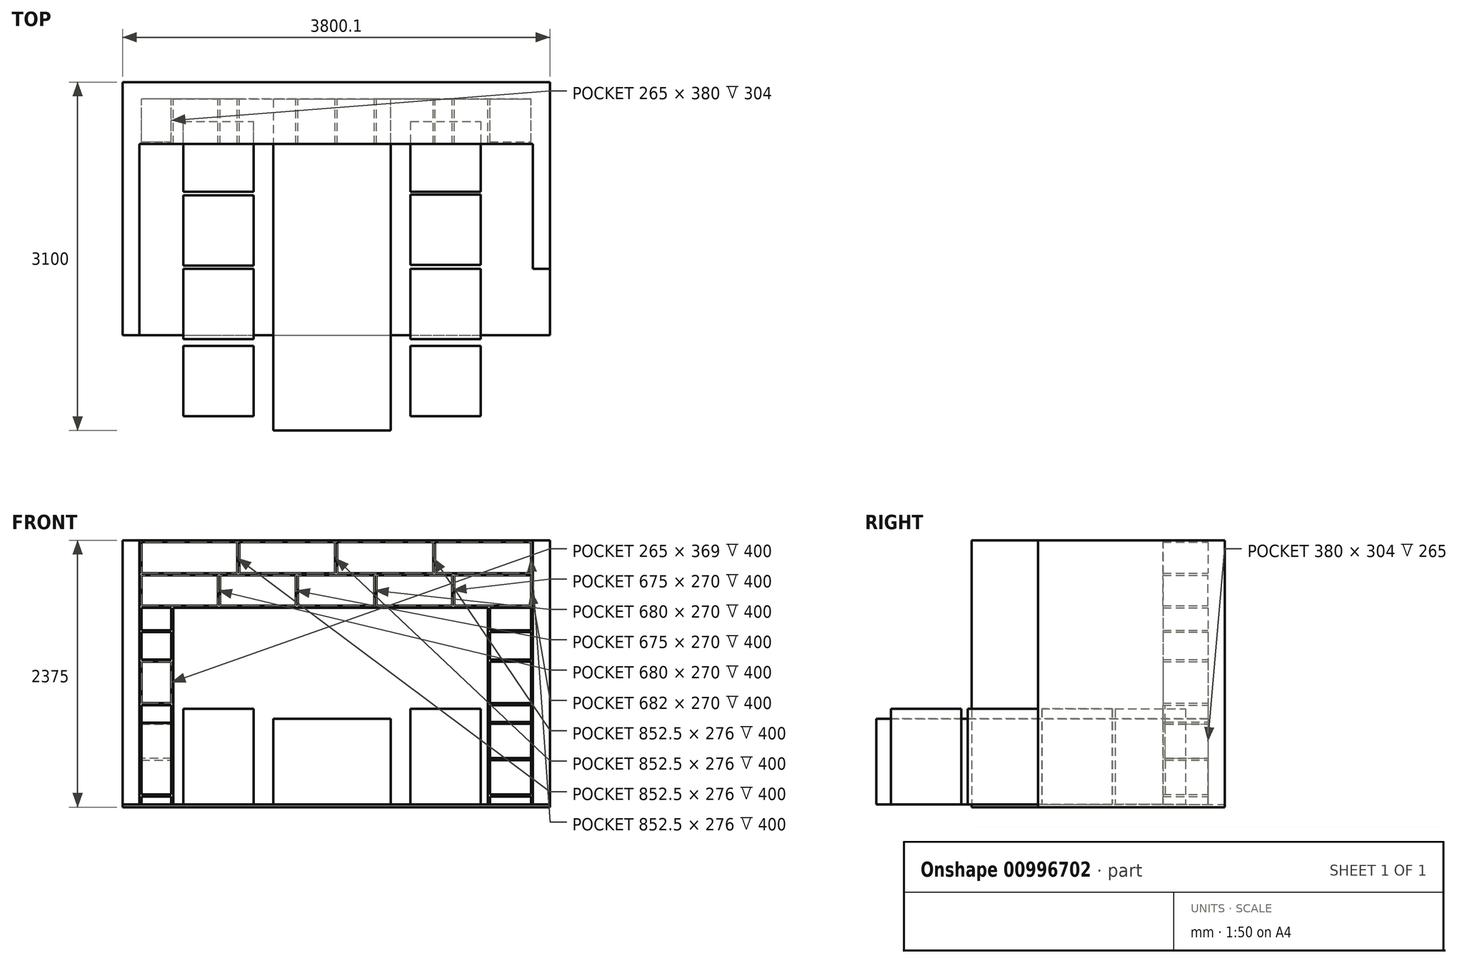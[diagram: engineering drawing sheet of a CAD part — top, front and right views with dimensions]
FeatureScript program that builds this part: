
annotation { "Feature Type Name" : "Feature", "Feature Type Description" : "" }
export const myFeature = defineFeature(function(context is Context, id is Id, definition is map)
    precondition{}
    {
        {
            var Q0;
            Q0=qCreatedBy(makeId("Top.planeOp"),FACE);
            var sketch = newSketch(context, id + "F0", { "sketchPlane" : qUnion([Q0])});
            skLineSegment(sketch, "E0", {"start": v(0, 0) * mm, "end": v(-1750, 0) * mm});
            skLineSegment(sketch, "E1", {"start": v(0, 0) * mm, "end": v(1750, 0) * mm});
            skLineSegment(sketch, "E2", {"start": v(-1750, 0) * mm, "end": v(-1750, -2100) * mm});
            skLineSegment(sketch, "E3", {"start": v(1750, 0) * mm, "end": v(1750, -1510) * mm});
            skLineSegment(sketch, "E4", {"start": v(-1750, -2100) * mm, "end": v(-1900, -2100) * mm});
            skLineSegment(sketch, "E5", {"start": v(-1900, -2100) * mm, "end": v(-1900, 150) * mm});
            skLineSegment(sketch, "E6", {"start": v(-1900, 150) * mm, "end": v(1900, 150) * mm});
            skLineSegment(sketch, "E7", {"start": v(1900, 150) * mm, "end": v(1900, -1510) * mm});
            skLineSegment(sketch, "E8", {"start": v(1900, -1510) * mm, "end": v(1750, -1510) * mm});
            skSolve(sketch);
        }
        {
            var Q0;
            Q0 = qSketchRegion(id + "F0", true);
            extrude(context, id + "F1", {"entities" : qUnion([Q0]), "depth" : 2375 * mm, "offsetDistance" : 25 * mm});
        }
        {
            var Q0;
            Q0=makeQuery(id+"F0.imprint","IMPRINT",FACE,{"disambiguationData":[TD([[makeQuery(id+"F0.imprint","IMPRINT",EDGE,{"derivedFrom":sQuery(id+"F0.wireOp",EDGE,"E0")}),-1.0]])]});
            var sketch = newSketch(context, id + "F2", { "sketchPlane" : qUnion([Q0])});
            skLineSegment(sketch, "E9.bottom", {"start": v(-1900.1, -2100.2) * mm, "end": v(1899.9, -2100.2) * mm});
            skLineSegment(sketch, "E9.top", {"start": v(-1900.1, 149.8) * mm, "end": v(1899.9, 149.8) * mm});
            skLineSegment(sketch, "E9.left", {"start": v(-1900.1, -2100.2) * mm, "end": v(-1900.1, 149.8) * mm});
            skLineSegment(sketch, "E9.right", {"start": v(1899.9, -2100.2) * mm, "end": v(1899.9, 149.8) * mm});
            skSolve(sketch);
        }
        {
            var Q0;
            {var subQ2=sQuery(id+"F2.wireOp",EDGE,"E9.bottom");Q0=makeQuery(id+"F2.imprint","IMPRINT",FACE,{"disambiguationData":[TD([[makeQuery(id+"F2.imprint","IMPRINT",EDGE,{"derivedFrom":subQ2}),1.0]])]});}
            extrude(context, id + "F3", {"entities" : qUnion([Q0]), "operationType" : NewBodyOperationType.ADD, "depth" : 25 * mm, "offsetDistance" : 25 * mm});
        }
        {
            var Q0;
            Q0=makeQuery(id+"F3.opExtrude","CAP_FACE",FACE,{"disambiguationData":[OSD([sQuery(id+"F0.wireOp",EDGE,"E0"),sQuery(id+"F0.wireOp",EDGE,"E1"),sQuery(id+"F0.wireOp",EDGE,"E2"),sQuery(id+"F0.wireOp",EDGE,"E3"),sQuery(id+"F0.wireOp",EDGE,"E4"),sQuery(id+"F0.wireOp",EDGE,"E5"),sQuery(id+"F0.wireOp",EDGE,"E8"),sQuery(id+"F2.wireOp",EDGE,"E9.bottom"),sQuery(id+"F2.wireOp",EDGE,"E9.top"),sQuery(id+"F2.wireOp",EDGE,"E9.left"),sQuery(id+"F2.wireOp",EDGE,"E9.right")])],"isStart":false});
            var sketch = newSketch(context, id + "F4", { "sketchPlane" : qUnion([Q0])});
            skLineSegment(sketch, "E10", {"start": v(-560, 0) * mm, "end": v(-560, -2950) * mm});
            skLineSegment(sketch, "E11", {"start": v(-560, -2950) * mm, "end": v(485, -2950) * mm});
            skLineSegment(sketch, "E12", {"start": v(485, -2950) * mm, "end": v(485, 0) * mm});
            skLineSegment(sketch, "E13", {"start": v(485, 0) * mm, "end": v(-560, 0) * mm});
            skSolve(sketch);
        }
        {
            var Q0;
            {var subQ0=sQuery(id+"F4.wireOp",EDGE,"E13");Q0=makeQuery(id+"F4.imprint","IMPRINT",FACE,{"disambiguationData":[TD([[makeQuery(id+"F4.imprint","IMPRINT",EDGE,{"derivedFrom":subQ0}),-1.0]])]});}
            var Q1;
            {var subQ0=sQuery(id+"F4.wireOp",EDGE,"E11");Q1=makeQuery(id+"F4.imprint","IMPRINT",FACE,{"disambiguationData":[TD([[makeQuery(id+"F4.imprint","IMPRINT",EDGE,{"derivedFrom":subQ0}),1.0]])]});}
            extrude(context, id + "F5", {"entities" : qUnion([Q0, Q1]), "operationType" : NewBodyOperationType.ADD, "depth" : 760 * mm, "offsetDistance" : 25 * mm});
        }
        {
            var Q0;
            {var subQ0=sQuery(id+"F0.wireOp",EDGE,"E5");var subQ2=sQuery(id+"F0.wireOp",EDGE,"E2");var subQ3=sQuery(id+"F0.wireOp",EDGE,"E4");var subQ4=sQuery(id+"F2.wireOp",EDGE,"E9.left");var subQ5=sQuery(id+"F0.wireOp",EDGE,"E1");var subQ6=sQuery(id+"F0.wireOp",EDGE,"E0");var subQ7=sQuery(id+"F2.wireOp",EDGE,"E9.bottom");var subQ8=sQuery(id+"F2.wireOp",EDGE,"E9.top");Q0=makeQuery(id+"F5.boolean.opBoolean","SPLIT",FACE,{"disambiguationData":[TD([makeQuery(id+"F1.opExtrude","SWEPT_FACE",FACE,{"disambiguationData":[OSD([subQ2])]})])],"derivedFrom":makeQuery(id+"F3.opExtrude","CAP_FACE",FACE,{"disambiguationData":[OSD([subQ6,subQ5,subQ2,sQuery(id+"F0.wireOp",EDGE,"E3"),subQ3,subQ0,sQuery(id+"F0.wireOp",EDGE,"E8"),subQ7,subQ8,subQ4,sQuery(id+"F2.wireOp",EDGE,"E9.right")])],"isStart":false})});}
            var sketch = newSketch(context, id + "F6", { "sketchPlane" : qUnion([Q0])});
            skLineSegment(sketch, "E14.bottom", {"start": v(-735, -2820) * mm, "end": v(-1360, -2820) * mm});
            skLineSegment(sketch, "E14.top", {"start": v(-735, -2195) * mm, "end": v(-1360, -2195) * mm});
            skLineSegment(sketch, "E14.left", {"start": v(-735, -2820) * mm, "end": v(-735, -2195) * mm});
            skLineSegment(sketch, "E14.right", {"start": v(-1360, -2820) * mm, "end": v(-1360, -2195) * mm});
            skLineSegment(sketch, "E15.bottom", {"start": v(-1360, -2135) * mm, "end": v(-735, -2135) * mm});
            skLineSegment(sketch, "E15.top", {"start": v(-1360, -1510) * mm, "end": v(-735, -1510) * mm});
            skLineSegment(sketch, "E15.left", {"start": v(-1360, -2135) * mm, "end": v(-1360, -1510) * mm});
            skLineSegment(sketch, "E15.right", {"start": v(-735, -2135) * mm, "end": v(-735, -1510) * mm});
            skLineSegment(sketch, "E16.bottom", {"start": v(-1360, -1480) * mm, "end": v(-735, -1480) * mm});
            skLineSegment(sketch, "E16.top", {"start": v(-1360, -855) * mm, "end": v(-735, -855) * mm});
            skLineSegment(sketch, "E16.left", {"start": v(-1360, -1480) * mm, "end": v(-1360, -855) * mm});
            skLineSegment(sketch, "E16.right", {"start": v(-735, -1480) * mm, "end": v(-735, -855) * mm});
            skLineSegment(sketch, "E17.bottom", {"start": v(-1360, -825) * mm, "end": v(-735, -825) * mm});
            skLineSegment(sketch, "E17.top", {"start": v(-1360, -200) * mm, "end": v(-735, -200) * mm});
            skLineSegment(sketch, "E17.left", {"start": v(-1360, -825) * mm, "end": v(-1360, -200) * mm});
            skLineSegment(sketch, "E17.right", {"start": v(-735, -825) * mm, "end": v(-735, -200) * mm});
            skLineSegment(sketch, "E18.bottom", {"start": v(660, -200) * mm, "end": v(1285, -200) * mm});
            skLineSegment(sketch, "E18.top", {"start": v(660, -825) * mm, "end": v(1285, -825) * mm});
            skLineSegment(sketch, "E18.left", {"start": v(660, -200) * mm, "end": v(660, -825) * mm});
            skLineSegment(sketch, "E18.right", {"start": v(1285, -200) * mm, "end": v(1285, -825) * mm});
            skLineSegment(sketch, "E19.bottom", {"start": v(660, -850) * mm, "end": v(1285, -850) * mm});
            skLineSegment(sketch, "E19.top", {"start": v(660, -1475) * mm, "end": v(1285, -1475) * mm});
            skLineSegment(sketch, "E19.left", {"start": v(660, -850) * mm, "end": v(660, -1475) * mm});
            skLineSegment(sketch, "E19.right", {"start": v(1285, -850) * mm, "end": v(1285, -1475) * mm});
            skLineSegment(sketch, "E20.bottom", {"start": v(660, -1510) * mm, "end": v(1285, -1510) * mm});
            skLineSegment(sketch, "E20.top", {"start": v(660, -2135) * mm, "end": v(1285, -2135) * mm});
            skLineSegment(sketch, "E20.left", {"start": v(660, -1510) * mm, "end": v(660, -2135) * mm});
            skLineSegment(sketch, "E20.right", {"start": v(1285, -1510) * mm, "end": v(1285, -2135) * mm});
            skLineSegment(sketch, "E21.bottom", {"start": v(660, -2195) * mm, "end": v(1285, -2195) * mm});
            skLineSegment(sketch, "E21.top", {"start": v(660, -2820) * mm, "end": v(1285, -2820) * mm});
            skLineSegment(sketch, "E21.left", {"start": v(660, -2195) * mm, "end": v(660, -2820) * mm});
            skLineSegment(sketch, "E21.right", {"start": v(1285, -2195) * mm, "end": v(1285, -2820) * mm});
            skSolve(sketch);
        }
        {
            var Q0;
            Q0 = qSketchRegion(id + "F6", true);
            extrude(context, id + "F7", {"entities" : qUnion([Q0]), "operationType" : NewBodyOperationType.ADD, "depth" : 850 * mm, "offsetDistance" : 25 * mm});
        }
        {
            var Q0;
            Q0=makeQuery(id+"F1.opExtrude","SWEPT_FACE",FACE,{"disambiguationData":[OSD([sQuery(id+"F0.wireOp",EDGE,"E0"),sQuery(id+"F0.wireOp",EDGE,"E1")])]});
            var sketch = newSketch(context, id + "F8", { "sketchPlane" : qUnion([Q0])});
            skLineSegment(sketch, "E22", {"start": v(-1750, 2375) * mm, "end": v(1750, 2375) * mm});
            skLineSegment(sketch, "E23", {"start": v(1750, 2375) * mm, "end": v(1750, 2357) * mm});
            skLineSegment(sketch, "E24", {"start": v(1750, 2357) * mm, "end": v(-1750, 2357) * mm});
            skLineSegment(sketch, "E25", {"start": v(-1750, 2357) * mm, "end": v(-1750, 2375) * mm});
            skLineSegment(sketch, "E26", {"start": v(-1750, 1775) * mm, "end": v(1750, 1775) * mm});
            skLineSegment(sketch, "E27", {"start": v(1750, 1775) * mm, "end": v(1750, 1793) * mm});
            skLineSegment(sketch, "E28", {"start": v(1750, 1793) * mm, "end": v(-1750, 1793) * mm});
            skLineSegment(sketch, "E29", {"start": v(-1750, 1793) * mm, "end": v(-1750, 1775) * mm});
            skLineSegment(sketch, "E30.bottom", {"start": v(-1467, 1775) * mm, "end": v(-1449, 1775) * mm});
            skLineSegment(sketch, "E30.top", {"start": v(-1467, 25) * mm, "end": v(-1449, 25) * mm});
            skLineSegment(sketch, "E30.left", {"start": v(-1467, 1775) * mm, "end": v(-1467, 25) * mm});
            skLineSegment(sketch, "E30.right", {"start": v(-1449, 1775) * mm, "end": v(-1449, 25) * mm});
            skLineSegment(sketch, "E31.bottom", {"start": v(1349, 1775) * mm, "end": v(1367, 1775) * mm});
            skLineSegment(sketch, "E31.top", {"start": v(1349, 25) * mm, "end": v(1367, 25) * mm});
            skLineSegment(sketch, "E31.left", {"start": v(1349, 1775) * mm, "end": v(1349, 25) * mm});
            skLineSegment(sketch, "E31.right", {"start": v(1367, 1775) * mm, "end": v(1367, 25) * mm});
            skLineSegment(sketch, "E32.bottom", {"start": v(-1750, 25) * mm, "end": v(-1732, 25) * mm});
            skLineSegment(sketch, "E32.top", {"start": v(-1750, 1775) * mm, "end": v(-1732, 1775) * mm});
            skLineSegment(sketch, "E32.left", {"start": v(-1750, 25) * mm, "end": v(-1750, 1775) * mm});
            skLineSegment(sketch, "E32.right", {"start": v(-1732, 25) * mm, "end": v(-1732, 1775) * mm});
            skLineSegment(sketch, "E33.bottom", {"start": v(1750, 25) * mm, "end": v(1732, 25) * mm});
            skLineSegment(sketch, "E33.top", {"start": v(1750, 1775) * mm, "end": v(1732, 1775) * mm});
            skLineSegment(sketch, "E33.left", {"start": v(1750, 25) * mm, "end": v(1750, 1775) * mm});
            skLineSegment(sketch, "E33.right", {"start": v(1732, 25) * mm, "end": v(1732, 1775) * mm});
            skLineSegment(sketch, "E34.bottom", {"start": v(1750, 1793) * mm, "end": v(1732, 1793) * mm});
            skLineSegment(sketch, "E34.top", {"start": v(1750, 2357) * mm, "end": v(1732, 2357) * mm});
            skLineSegment(sketch, "E34.left", {"start": v(1750, 1793) * mm, "end": v(1750, 2357) * mm});
            skLineSegment(sketch, "E34.right", {"start": v(1732, 1793) * mm, "end": v(1732, 2357) * mm});
            skLineSegment(sketch, "E35.bottom", {"start": v(-1732, 1793) * mm, "end": v(-1750, 1793) * mm});
            skLineSegment(sketch, "E35.top", {"start": v(-1732, 2375) * mm, "end": v(-1750, 2375) * mm});
            skLineSegment(sketch, "E35.left", {"start": v(-1732, 1793) * mm, "end": v(-1732, 2375) * mm});
            skLineSegment(sketch, "E35.right", {"start": v(-1750, 1793) * mm, "end": v(-1750, 2375) * mm});
            skSolve(sketch);
        }
        {
            var Q0;
            {var subQ6=sQuery(id+"F8.wireOp",EDGE,"E34.left");var subQ8=sQuery(id+"F8.wireOp",EDGE,"E23");var subQ13=sQuery(id+"F8.wireOp",EDGE,"E27");var subQ25=sQuery(id+"F8.wireOp",EDGE,"E35.right");var subQ26=sQuery(id+"F8.wireOp",EDGE,"E25");Q0=qUnion([makeQuery(id+"F8.imprint","IMPRINT",FACE,{"disambiguationData":[TD([[makeQuery(id+"F8.imprint","IMPRINT",EDGE,{"derivedFrom":subQ13}),-1.0]])]}),makeQuery(id+"F8.imprint","IMPRINT",FACE,{"disambiguationData":[TD([[makeQuery(id+"F8.imprint","IMPRINT",EDGE,{"derivedFrom":subQ8}),-1.0]])]}),makeQuery(id+"F8.imprint","IMPRINT",FACE,{"disambiguationData":[TD([[makeQuery(id+"F8.imprint","IMPRINT",EDGE,{"derivedFrom":sQuery(id+"F8.wireOp",EDGE,"E30.top")}),1.0]])]}),makeQuery(id+"F8.imprint","IMPRINT",FACE,{"disambiguationData":[TD([[makeQuery(id+"F8.imprint","IMPRINT",EDGE,{"derivedFrom":subQ26}),1.0]])]}),makeQuery(id+"F8.imprint","IMPRINT",FACE,{"disambiguationData":[TD([[makeQuery(id+"F8.imprint","IMPRINT",EDGE,{"derivedFrom":subQ25}),1.0]])]}),makeQuery(id+"F8.imprint","IMPRINT",FACE,{"disambiguationData":[TD([[makeQuery(id+"F8.imprint","IMPRINT",EDGE,{"derivedFrom":sQuery(id+"F8.wireOp",EDGE,"E31.top")}),1.0]])]}),makeQuery(id+"F8.imprint","IMPRINT",FACE,{"disambiguationData":[TD([[makeQuery(id+"F8.imprint","IMPRINT",EDGE,{"derivedFrom":sQuery(id+"F8.wireOp",EDGE,"E33.bottom")}),1.0]])]}),makeQuery(id+"F8.imprint","IMPRINT",FACE,{"disambiguationData":[TD([[makeQuery(id+"F8.imprint","IMPRINT",EDGE,{"derivedFrom":subQ6}),-1.0]])]}),makeQuery(id+"F8.imprint","IMPRINT",FACE,{"disambiguationData":[TD([[makeQuery(id+"F8.imprint","IMPRINT",EDGE,{"derivedFrom":sQuery(id+"F8.wireOp",EDGE,"E32.bottom")}),1.0]])]})]);}
            extrude(context, id + "F9", {"entities" : qUnion([Q0]), "operationType" : NewBodyOperationType.ADD, "depth" : 400 * mm, "offsetDistance" : 25 * mm});
        }
        {
            var Q0;
            Q0=makeQuery(id+"F9.boolean.opBoolean","SPLIT",FACE,{"disambiguationData":[TD([makeQuery(id+"F9.opExtrude","SWEPT_FACE",FACE,{"disambiguationData":[OSD([sQuery(id+"F8.wireOp",EDGE,"E24")])]})])],"derivedFrom":makeQuery(id+"F1.opExtrude","SWEPT_FACE",FACE,{"disambiguationData":[OSD([sQuery(id+"F0.wireOp",EDGE,"E0"),sQuery(id+"F0.wireOp",EDGE,"E1")])]})});
            var sketch = newSketch(context, id + "F10", { "sketchPlane" : qUnion([Q0])});
            skLineSegment(sketch, "E36", {"start": v(1732, 2075) * mm, "end": v(1732, 2081) * mm});
            skLineSegment(sketch, "E37", {"start": v(1732, 2081) * mm, "end": v(-1732, 2081) * mm});
            skLineSegment(sketch, "E38", {"start": v(-1732, 2081) * mm, "end": v(-1732, 2063) * mm});
            skLineSegment(sketch, "E39", {"start": v(-1732, 2063) * mm, "end": v(1732, 2063) * mm});
            skLineSegment(sketch, "E40", {"start": v(1732, 2063) * mm, "end": v(1732, 2081) * mm});
            skSolve(sketch);
        }
        {
            var Q0;
            {var subQ0=sQuery(id+"F10.wireOp",EDGE,"E37");Q0=makeQuery(id+"F10.imprint","IMPRINT",FACE,{"disambiguationData":[TD([[makeQuery(id+"F10.imprint","IMPRINT",EDGE,{"derivedFrom":subQ0}),1.0]])]});}
            extrude(context, id + "F11", {"entities" : qUnion([Q0]), "operationType" : NewBodyOperationType.ADD, "depth" : 400 * mm, "offsetDistance" : 25 * mm});
        }
        {
            var Q0;
            {var subQ0=makeQuery(id+"F9.opExtrude","SWEPT_FACE",FACE,{"disambiguationData":[OSD([sQuery(id+"F8.wireOp",EDGE,"E24")])]});Q0=makeQuery(id+"F11.boolean.opBoolean","SPLIT",FACE,{"disambiguationData":[TD([subQ0])],"derivedFrom":makeQuery(id+"F9.boolean.opBoolean","SPLIT",FACE,{"disambiguationData":[TD([subQ0])],"derivedFrom":makeQuery(id+"F1.opExtrude","SWEPT_FACE",FACE,{"disambiguationData":[OSD([sQuery(id+"F0.wireOp",EDGE,"E0"),sQuery(id+"F0.wireOp",EDGE,"E1")])]})})});}
            var sketch = newSketch(context, id + "F12", { "sketchPlane" : qUnion([Q0])});
            skLineSegment(sketch, "E41", {"start": v(0, 2081) * mm, "end": v(9, 2081) * mm});
            skLineSegment(sketch, "E42", {"start": v(9, 2081) * mm, "end": v(9, 2357) * mm});
            skLineSegment(sketch, "E43", {"start": v(9, 2357) * mm, "end": v(-9, 2357) * mm});
            skLineSegment(sketch, "E44", {"start": v(-9, 2357) * mm, "end": v(-9, 2081) * mm});
            skLineSegment(sketch, "E45", {"start": v(-9, 2081) * mm, "end": v(9, 2081) * mm});
            skLineSegment(sketch, "E46", {"start": v(-879.5, 2357) * mm, "end": v(-879.5, 2081) * mm});
            skLineSegment(sketch, "E47", {"start": v(-879.5, 2081) * mm, "end": v(-861.5, 2081) * mm});
            skLineSegment(sketch, "E48", {"start": v(-861.5, 2081) * mm, "end": v(-861.5, 2357) * mm});
            skLineSegment(sketch, "E49", {"start": v(-861.5, 2357) * mm, "end": v(-879.5, 2357) * mm});
            skLineSegment(sketch, "E50", {"start": v(879.5, 2081) * mm, "end": v(879.5, 2357) * mm});
            skLineSegment(sketch, "E51", {"start": v(879.5, 2357) * mm, "end": v(861.5, 2357) * mm});
            skLineSegment(sketch, "E52", {"start": v(861.5, 2357) * mm, "end": v(861.5, 2081) * mm});
            skLineSegment(sketch, "E53", {"start": v(861.5, 2081) * mm, "end": v(879.5, 2081) * mm});
            skSolve(sketch);
        }
        {
            var Q0;
            Q0 = qSketchRegion(id + "F12", true);
            extrude(context, id + "F13", {"entities" : qUnion([Q0]), "operationType" : NewBodyOperationType.ADD, "depth" : 400 * mm, "offsetDistance" : 25 * mm});
        }
        {
            var Q0;
            {var subQ0=makeQuery(id+"F9.opExtrude","SWEPT_FACE",FACE,{"disambiguationData":[OSD([sQuery(id+"F8.wireOp",EDGE,"E28")])]});Q0=makeQuery(id+"F11.boolean.opBoolean","SPLIT",FACE,{"disambiguationData":[TD([subQ0])],"derivedFrom":makeQuery(id+"F9.boolean.opBoolean","SPLIT",FACE,{"disambiguationData":[TD([makeQuery(id+"F9.opExtrude","SWEPT_FACE",FACE,{"disambiguationData":[OSD([sQuery(id+"F8.wireOp",EDGE,"E24")])]})])],"derivedFrom":makeQuery(id+"F1.opExtrude","SWEPT_FACE",FACE,{"disambiguationData":[OSD([sQuery(id+"F0.wireOp",EDGE,"E0"),sQuery(id+"F0.wireOp",EDGE,"E1")])]})})});}
            var sketch = newSketch(context, id + "F14", { "sketchPlane" : qUnion([Q0])});
            skLineSegment(sketch, "E54", {"start": v(1032, 1793) * mm, "end": v(847.37, 1793) * mm});
            skLineSegment(sketch, "E55", {"start": v(1032, 1793) * mm, "end": v(1032, 2063) * mm});
            skLineSegment(sketch, "E56", {"start": v(1032, 2063) * mm, "end": v(1050, 2063) * mm});
            skLineSegment(sketch, "E57", {"start": v(1050, 2063) * mm, "end": v(1050, 1793) * mm});
            skLineSegment(sketch, "E58", {"start": v(1050, 1793) * mm, "end": v(1032, 1793) * mm});
            skLineSegment(sketch, "E59", {"start": v(-866, 1793) * mm, "end": v(-1052, 1793) * mm});
            skLineSegment(sketch, "E60", {"start": v(-1052, 1793) * mm, "end": v(-1052, 2063) * mm});
            skLineSegment(sketch, "E61", {"start": v(-1052, 2063) * mm, "end": v(-1034, 2063) * mm});
            skLineSegment(sketch, "E62", {"start": v(-1034, 2063) * mm, "end": v(-1034, 1793) * mm});
            skLineSegment(sketch, "E63", {"start": v(-1034, 1793) * mm, "end": v(-1052, 1793) * mm});
            skLineSegment(sketch, "E64", {"start": v(-341, 2063) * mm, "end": v(-341, 1793) * mm});
            skLineSegment(sketch, "E65", {"start": v(-341, 1793) * mm, "end": v(-359, 1793) * mm});
            skLineSegment(sketch, "E66", {"start": v(-359, 1793) * mm, "end": v(-359, 2063) * mm});
            skLineSegment(sketch, "E67", {"start": v(-359, 2063) * mm, "end": v(-341, 2063) * mm});
            skLineSegment(sketch, "E68", {"start": v(339, 2063) * mm, "end": v(339, 1793) * mm});
            skLineSegment(sketch, "E69", {"start": v(339, 1793) * mm, "end": v(357, 1793) * mm});
            skLineSegment(sketch, "E70", {"start": v(357, 1793) * mm, "end": v(357, 2063) * mm});
            skLineSegment(sketch, "E71", {"start": v(357, 2063) * mm, "end": v(339, 2063) * mm});
            skSolve(sketch);
        }
        {
            var Q0;
            {var subQ0=sQuery(id+"F14.wireOp",EDGE,"E60");Q0=qUnion([makeQuery(id+"F14.imprint","IMPRINT",FACE,{"disambiguationData":[TD([[makeQuery(id+"F14.imprint","IMPRINT",EDGE,{"derivedFrom":sQuery(id+"F14.wireOp",EDGE,"E55")}),-1.0]])]}),makeQuery(id+"F14.imprint","IMPRINT",FACE,{"disambiguationData":[TD([[makeQuery(id+"F14.imprint","IMPRINT",EDGE,{"derivedFrom":subQ0}),-1.0]])]}),makeQuery(id+"F14.imprint","IMPRINT",FACE,{"disambiguationData":[TD([[makeQuery(id+"F14.imprint","IMPRINT",EDGE,{"derivedFrom":sQuery(id+"F14.wireOp",EDGE,"E64")}),-1.0]])]}),makeQuery(id+"F14.imprint","IMPRINT",FACE,{"disambiguationData":[TD([[makeQuery(id+"F14.imprint","IMPRINT",EDGE,{"derivedFrom":sQuery(id+"F14.wireOp",EDGE,"E68")}),1.0]])]})]);}
            extrude(context, id + "F15", {"entities" : qUnion([Q0]), "operationType" : NewBodyOperationType.ADD, "depth" : 400 * mm, "offsetDistance" : 25 * mm});
        }
        {
            var Q0;
            {var subQ0=sQuery(id+"F0.wireOp",EDGE,"E1");var subQ1=sQuery(id+"F0.wireOp",EDGE,"E0");var subQ4=sQuery(id+"F8.wireOp",EDGE,"E30.left");Q0=makeQuery(id+"F9.boolean.opBoolean","SPLIT",FACE,{"disambiguationData":[TD([makeQuery(id+"F9.opExtrude","SWEPT_FACE",FACE,{"disambiguationData":[OSD([subQ4])]})])],"derivedFrom":makeQuery(id+"F1.opExtrude","SWEPT_FACE",FACE,{"disambiguationData":[OSD([subQ1,subQ0])]})});}
            var sketch = newSketch(context, id + "F16", { "sketchPlane" : qUnion([Q0])});
            skPoint(sketch, "E72", {"position": v(-1467, 925) * mm});
            skLineSegment(sketch, "E73", {"start": v(-1467, 925) * mm, "end": v(-1732, 925) * mm});
            skLineSegment(sketch, "E74", {"start": v(-1732, 925) * mm, "end": v(-1732, 739) * mm});
            skLineSegment(sketch, "E75", {"start": v(-1732, 739) * mm, "end": v(-1467, 739) * mm});
            skLineSegment(sketch, "E76", {"start": v(-1467, 739) * mm, "end": v(-1467, 925) * mm});
            skLineSegment(sketch, "E77", {"start": v(-1732, 757) * mm, "end": v(-1467, 757) * mm});
            skLineSegment(sketch, "E78", {"start": v(-1467, 757) * mm, "end": v(-1467, 739) * mm});
            skLineSegment(sketch, "E79", {"start": v(-1732, 739) * mm, "end": v(-1732, 757) * mm});
            skLineSegment(sketch, "E80", {"start": v(-1732, 925) * mm, "end": v(-1732, 907) * mm});
            skLineSegment(sketch, "E81", {"start": v(-1732, 907) * mm, "end": v(-1467, 907) * mm});
            skLineSegment(sketch, "E82", {"start": v(-1467, 907) * mm, "end": v(-1467, 925) * mm});
            skLineSegment(sketch, "E83", {"start": v(-1467, 435) * mm, "end": v(-1732, 435) * mm});
            skLineSegment(sketch, "E84", {"start": v(-1732, 435) * mm, "end": v(-1732, 417) * mm});
            skLineSegment(sketch, "E85", {"start": v(-1732, 417) * mm, "end": v(-1467, 417) * mm});
            skLineSegment(sketch, "E86", {"start": v(-1467, 417) * mm, "end": v(-1467, 435) * mm});
            skLineSegment(sketch, "E87", {"start": v(-1732, 113) * mm, "end": v(-1467, 113) * mm});
            skLineSegment(sketch, "E88", {"start": v(-1467, 113) * mm, "end": v(-1467, 95) * mm});
            skLineSegment(sketch, "E89", {"start": v(-1467, 95) * mm, "end": v(-1732, 95) * mm});
            skLineSegment(sketch, "E90", {"start": v(-1732, 95) * mm, "end": v(-1732, 113) * mm});
            skSolve(sketch);
        }
        {
            var Q0;
            {var subQ0=sQuery(id+"F16.wireOp",EDGE,"E73");Q0=makeQuery(id+"F16.imprint","IMPRINT",FACE,{"disambiguationData":[TD([[makeQuery(id+"F16.imprint","IMPRINT",EDGE,{"derivedFrom":subQ0}),1.0]])]});}
            var Q1;
            {var subQ0=sQuery(id+"F16.wireOp",EDGE,"E75");Q1=makeQuery(id+"F16.imprint","IMPRINT",FACE,{"disambiguationData":[TD([[makeQuery(id+"F16.imprint","IMPRINT",EDGE,{"derivedFrom":subQ0}),1.0]])]});}
            var Q2;
            Q2=makeQuery(id+"F16.imprint","IMPRINT",FACE,{"disambiguationData":[TD([[makeQuery(id+"F16.imprint","IMPRINT",EDGE,{"derivedFrom":sQuery(id+"F16.wireOp",EDGE,"E83")}),1.0]])]});
            var Q3;
            Q3=makeQuery(id+"F16.imprint","IMPRINT",FACE,{"disambiguationData":[TD([[makeQuery(id+"F16.imprint","IMPRINT",EDGE,{"derivedFrom":sQuery(id+"F16.wireOp",EDGE,"E87")}),-1.0]])]});
            extrude(context, id + "F17", {"entities" : qUnion([Q0, Q1, Q2, Q3]), "operationType" : NewBodyOperationType.ADD, "depth" : 380 * mm, "offsetDistance" : 25 * mm});
        }
        {
            var Q0;
            Q0=makeQuery(id+"F17.opExtrude","CAP_FACE",FACE,{"disambiguationData":[OSD([sQuery(id+"F16.wireOp",EDGE,"E73"),sQuery(id+"F16.wireOp",EDGE,"E74"),sQuery(id+"F16.wireOp",EDGE,"E76"),sQuery(id+"F16.wireOp",EDGE,"E81")])],"isStart":false});
            var Q1;
            Q1=makeQuery(id+"F17.opExtrude","CAP_FACE",FACE,{"disambiguationData":[OSD([sQuery(id+"F16.wireOp",EDGE,"E87"),sQuery(id+"F16.wireOp",EDGE,"E88"),sQuery(id+"F16.wireOp",EDGE,"E89"),sQuery(id+"F16.wireOp",EDGE,"E90")])],"isStart":false});
            extrude(context, id + "F18", {"entities" : qUnion([Q0, Q1]), "operationType" : NewBodyOperationType.ADD, "depth" : 20 * mm, "offsetDistance" : 25 * mm});
        }
        {
            var Q0;
            {var subQ2=sQuery(id+"F8.wireOp",EDGE,"E30.left");var subQ4=makeQuery(id+"F9.opExtrude","SWEPT_FACE",FACE,{"disambiguationData":[OSD([subQ2])]});var subQ6=sQuery(id+"F0.wireOp",EDGE,"E1");var subQ7=sQuery(id+"F0.wireOp",EDGE,"E0");Q0=makeQuery(id+"F17.boolean.opBoolean","SPLIT",FACE,{"disambiguationData":[TD([makeQuery(id+"F17.opExtrude","SWEPT_FACE",FACE,{"disambiguationData":[OSD([sQuery(id+"F16.wireOp",EDGE,"E73")])]})])],"derivedFrom":makeQuery(id+"F9.boolean.opBoolean","SPLIT",FACE,{"disambiguationData":[TD([subQ4])],"derivedFrom":makeQuery(id+"F1.opExtrude","SWEPT_FACE",FACE,{"disambiguationData":[OSD([subQ7,subQ6])]})})});}
            var sketch = newSketch(context, id + "F19", { "sketchPlane" : qUnion([Q0])});
            skLineSegment(sketch, "E91", {"start": v(-1732, 1312) * mm, "end": v(-1467, 1312) * mm});
            skLineSegment(sketch, "E92", {"start": v(-1467, 1312) * mm, "end": v(-1467, 1294) * mm});
            skLineSegment(sketch, "E93", {"start": v(-1467, 1294) * mm, "end": v(-1732, 1294) * mm});
            skLineSegment(sketch, "E94", {"start": v(-1732, 1294) * mm, "end": v(-1732, 1312) * mm});
            skLineSegment(sketch, "E95", {"start": v(-1732, 1557) * mm, "end": v(-1467, 1557) * mm});
            skLineSegment(sketch, "E96", {"start": v(-1467, 1557) * mm, "end": v(-1467, 1575) * mm});
            skLineSegment(sketch, "E97", {"start": v(-1467, 1575) * mm, "end": v(-1732, 1575) * mm});
            skLineSegment(sketch, "E98", {"start": v(-1732, 1575) * mm, "end": v(-1732, 1557) * mm});
            skPoint(sketch, "E99", {"position": v(-1599.5, 1775) * mm});
            skPoint(sketch, "E100", {"position": v(-1599.5, 925) * mm});
            skSolve(sketch);
        }
        {
            var Q0;
            Q0 = qSketchRegion(id + "F19", true);
            extrude(context, id + "F20", {"entities" : qUnion([Q0]), "operationType" : NewBodyOperationType.ADD, "depth" : 400 * mm, "offsetDistance" : 25 * mm});
        }
        {
            var Q0;
            Q0=makeQuery(id+"F17.opExtrude","CAP_FACE",FACE,{"disambiguationData":[OSD([sQuery(id+"F16.wireOp",EDGE,"E74"),sQuery(id+"F16.wireOp",EDGE,"E75"),sQuery(id+"F16.wireOp",EDGE,"E76"),sQuery(id+"F16.wireOp",EDGE,"E77")])],"isStart":false});
            var sketch = newSketch(context, id + "F21", { "sketchPlane" : qUnion([Q0])});
            skPoint(sketch, "E101", {"position": v(-1732, 750.5) * mm});
            skPoint(sketch, "E102", {"position": v(-1732, 749) * mm});
            skPoint(sketch, "E103", {"position": v(-1732, 748) * mm});
            skLineSegment(sketch, "E104", {"start": v(-1732, 750.5) * mm, "end": v(-1467, 750.5) * mm});
            skLineSegment(sketch, "E105", {"start": v(-1467, 750.5) * mm, "end": v(-1467, 905.5) * mm});
            skLineSegment(sketch, "E106", {"start": v(-1467, 905.5) * mm, "end": v(-1732, 905.5) * mm});
            skLineSegment(sketch, "E107", {"start": v(-1732, 905.5) * mm, "end": v(-1732, 750.5) * mm});
            skLineSegment(sketch, "E108", {"start": v(-1732, 749) * mm, "end": v(-1467, 749) * mm});
            skLineSegment(sketch, "E109", {"start": v(-1467, 749) * mm, "end": v(-1467, 114) * mm});
            skLineSegment(sketch, "E110", {"start": v(-1467, 114) * mm, "end": v(-1732, 114) * mm});
            skLineSegment(sketch, "E111", {"start": v(-1732, 114) * mm, "end": v(-1732, 749) * mm});
            skSolve(sketch);
        }
        {
            var Q0;
            Q0 = qSketchRegion(id + "F21", true);
            extrude(context, id + "F22", {"entities" : qUnion([Q0]), "operationType" : NewBodyOperationType.ADD, "depth" : 18 * mm, "offsetDistance" : 25 * mm});
        }
        {
            var Q0;
            {var subQ0=sQuery(id+"F0.wireOp",EDGE,"E1");var subQ1=sQuery(id+"F0.wireOp",EDGE,"E0");var subQ2=sQuery(id+"F8.wireOp",EDGE,"E31.right");Q0=makeQuery(id+"F9.boolean.opBoolean","SPLIT",FACE,{"disambiguationData":[TD([makeQuery(id+"F9.opExtrude","SWEPT_FACE",FACE,{"disambiguationData":[OSD([subQ2])]})])],"derivedFrom":makeQuery(id+"F1.opExtrude","SWEPT_FACE",FACE,{"disambiguationData":[OSD([subQ1,subQ0])]})});}
            var sketch = newSketch(context, id + "F23", { "sketchPlane" : qUnion([Q0])});
            skLineSegment(sketch, "E112", {"start": v(1367, 1575) * mm, "end": v(1732, 1575) * mm});
            skLineSegment(sketch, "E113", {"start": v(1732, 1575) * mm, "end": v(1732, 1557) * mm});
            skLineSegment(sketch, "E114", {"start": v(1732, 1557) * mm, "end": v(1367, 1557) * mm});
            skLineSegment(sketch, "E115", {"start": v(1367, 1557) * mm, "end": v(1367, 1575) * mm});
            skLineSegment(sketch, "E116", {"start": v(1367, 1312) * mm, "end": v(1732, 1312) * mm});
            skLineSegment(sketch, "E117", {"start": v(1732, 1312) * mm, "end": v(1732, 1294) * mm});
            skLineSegment(sketch, "E118", {"start": v(1732, 1294) * mm, "end": v(1367, 1294) * mm});
            skLineSegment(sketch, "E119", {"start": v(1367, 1294) * mm, "end": v(1367, 1312) * mm});
            skLineSegment(sketch, "E120", {"start": v(1367, 95) * mm, "end": v(1732, 95) * mm});
            skLineSegment(sketch, "E121", {"start": v(1732, 95) * mm, "end": v(1732, 113) * mm});
            skLineSegment(sketch, "E122", {"start": v(1732, 113) * mm, "end": v(1367, 113) * mm});
            skLineSegment(sketch, "E123", {"start": v(1367, 113) * mm, "end": v(1367, 95) * mm});
            skPoint(sketch, "E124", {"position": v(1549.5, 25) * mm});
            skLineSegment(sketch, "E125", {"start": v(1367, 925) * mm, "end": v(1732, 925) * mm});
            skLineSegment(sketch, "E126", {"start": v(1732, 925) * mm, "end": v(1732, 907) * mm});
            skLineSegment(sketch, "E127", {"start": v(1732, 907) * mm, "end": v(1367, 907) * mm});
            skLineSegment(sketch, "E128", {"start": v(1367, 907) * mm, "end": v(1367, 925) * mm});
            skSolve(sketch);
        }
        {
            var Q0;
            Q0 = qSketchRegion(id + "F23", true);
            extrude(context, id + "F24", {"entities" : qUnion([Q0]), "operationType" : NewBodyOperationType.ADD, "depth" : 400 * mm, "offsetDistance" : 25 * mm});
        }
        {
            var Q0;
            {var subQ0=sQuery(id+"F8.wireOp",EDGE,"E31.right");var subQ1=makeQuery(id+"F9.opExtrude","SWEPT_FACE",FACE,{"disambiguationData":[OSD([subQ0])]});var subQ4=sQuery(id+"F0.wireOp",EDGE,"E1");var subQ5=sQuery(id+"F0.wireOp",EDGE,"E0");Q0=makeQuery(id+"F24.boolean.opBoolean","SPLIT",FACE,{"disambiguationData":[TD([makeQuery(id+"F24.opExtrude","SWEPT_FACE",FACE,{"disambiguationData":[OSD([sQuery(id+"F23.wireOp",EDGE,"E122")])]})])],"derivedFrom":makeQuery(id+"F9.boolean.opBoolean","SPLIT",FACE,{"disambiguationData":[TD([subQ1])],"derivedFrom":makeQuery(id+"F1.opExtrude","SWEPT_FACE",FACE,{"disambiguationData":[OSD([subQ5,subQ4])]})})});}
            var sketch = newSketch(context, id + "F25", { "sketchPlane" : qUnion([Q0])});
            skLineSegment(sketch, "E129", {"start": v(1367, 758.5) * mm, "end": v(1732, 758.5) * mm});
            skLineSegment(sketch, "E130", {"start": v(1732, 758.5) * mm, "end": v(1732, 740.5) * mm});
            skLineSegment(sketch, "E131", {"start": v(1732, 740.5) * mm, "end": v(1367, 740.5) * mm});
            skLineSegment(sketch, "E132", {"start": v(1367, 740.5) * mm, "end": v(1367, 758.5) * mm});
            skLineSegment(sketch, "E133", {"start": v(1367, 436.5) * mm, "end": v(1732, 436.5) * mm});
            skLineSegment(sketch, "E134", {"start": v(1732, 436.5) * mm, "end": v(1732, 418.5) * mm});
            skLineSegment(sketch, "E135", {"start": v(1732, 418.5) * mm, "end": v(1367, 418.5) * mm});
            skLineSegment(sketch, "E136", {"start": v(1367, 418.5) * mm, "end": v(1367, 436.5) * mm});
            skSolve(sketch);
        }
        {
            var Q0;
            Q0 = qSketchRegion(id + "F25", true);
            extrude(context, id + "F26", {"entities" : qUnion([Q0]), "operationType" : NewBodyOperationType.ADD, "depth" : 380 * mm, "offsetDistance" : 25 * mm});
        }
    });
